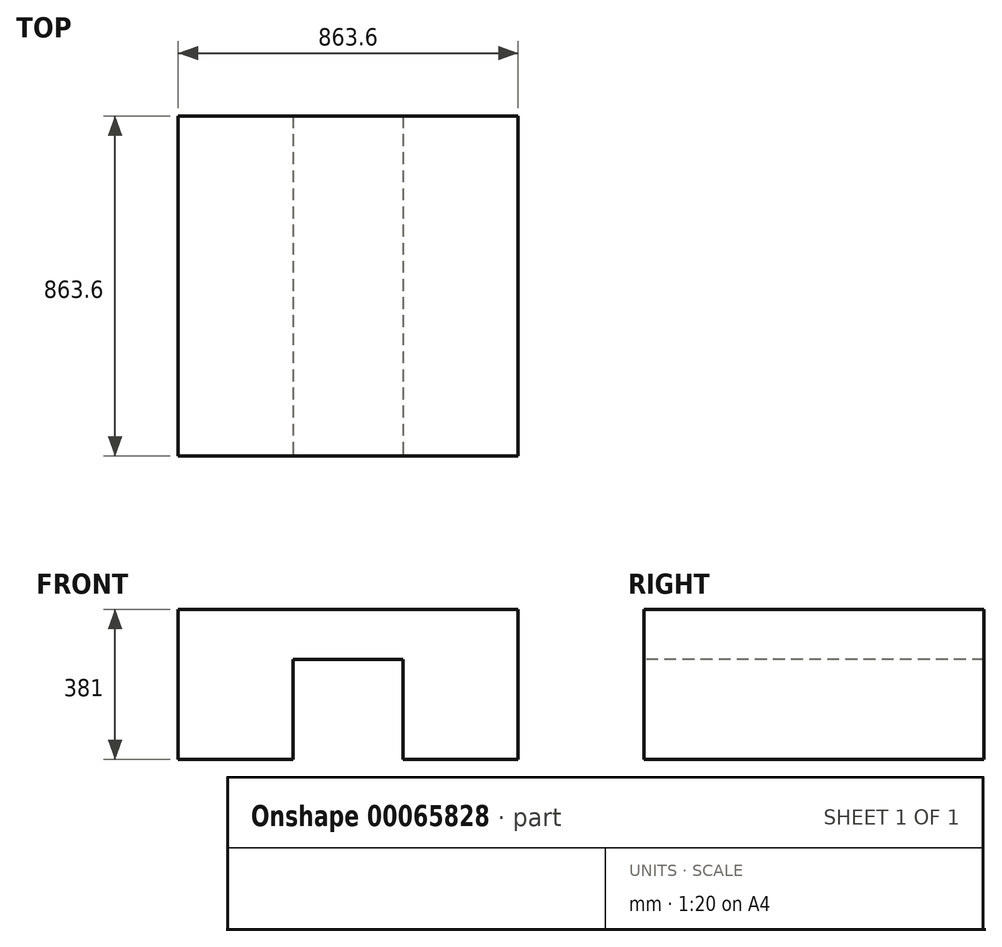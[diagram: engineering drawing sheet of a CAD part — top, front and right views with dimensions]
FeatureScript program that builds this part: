
annotation { "Feature Type Name" : "Feature", "Feature Type Description" : "" }
export const myFeature = defineFeature(function(context is Context, id is Id, definition is map)
    precondition{}
    {
        {
            var Q0;
            Q0=qCreatedBy(makeId("Front.planeOp"),FACE);
            var sketch = newSketch(context, id + "F0", { "sketchPlane" : qUnion([Q0])});
            skLineSegment(sketch, "E0.rect.bottom", {"start": v(-431.8, 190.5) * mm, "end": v(431.8, 190.5) * mm});
            skLineSegment(sketch, "E0.rect.top", {"start": v(-431.8, -190.5) * mm, "end": v(-139.7, -190.5) * mm});
            skLineSegment(sketch, "E0.rect.left", {"start": v(-431.8, 190.5) * mm, "end": v(-431.8, -190.5) * mm});
            skLineSegment(sketch, "E0.rect.right", {"start": v(431.8, 190.5) * mm, "end": v(431.8, -190.5) * mm});
            skPoint(sketch, "E0.rect.middle", {"position": v(0, 0) * mm});
            skLineSegment(sketch, "E1.rect.right", {"start": v(139.7, 63.5) * mm, "end": v(139.7, -190.5) * mm});
            skLineSegment(sketch, "E2.MirrorCS", {"start": v(-139.7, 63.5) * mm, "end": v(-139.7, -190.5) * mm});
            skLineSegment(sketch, "E3", {"start": v(-139.7, 63.5) * mm, "end": v(139.7, 63.5) * mm});
            skPoint(sketch, "E4.orphan", {"position": v(0, 190.5) * mm});
            skLineSegment(sketch, "E5.trimOffspring", {"start": v(139.7, -190.5) * mm, "end": v(431.8, -190.5) * mm});
            skSolve(sketch);
        }
        {
            var Q0;
            Q0=makeQuery(id+"F0.imprint","IMPRINT",FACE,{"disambiguationData":[TD([[makeQuery(id+"F0.imprint","IMPRINT",EDGE,{"derivedFrom":sQuery(id+"F0.wireOp",EDGE,"E0.rect.bottom")}),-1.0]])]});
            extrude(context, id + "F1", {"entities" : qUnion([Q0]), "oppositeDirection" : true, "depth" : 863.6 * mm});
        }
    });
